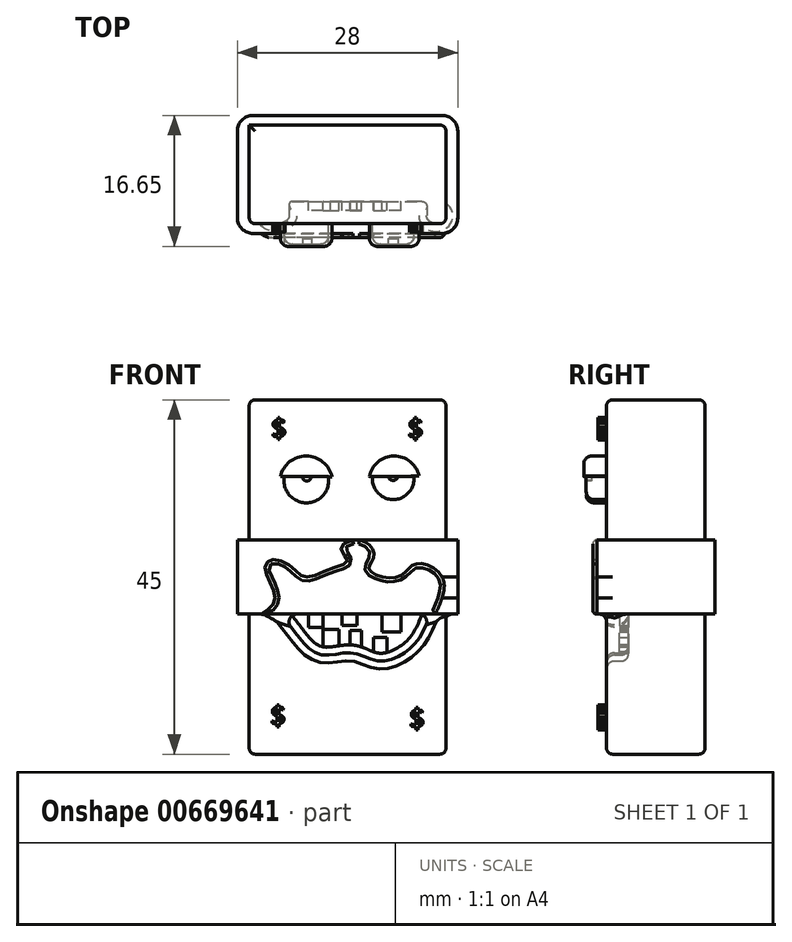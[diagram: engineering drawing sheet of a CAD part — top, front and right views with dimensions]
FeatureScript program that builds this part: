
annotation { "Feature Type Name" : "Feature", "Feature Type Description" : "" }
export const myFeature = defineFeature(function(context is Context, id is Id, definition is map)
    precondition{}
    {
        {
            var Q0;
            Q0=qCreatedBy(makeId("Front.planeOp"),FACE);
            var sketch = newSketch(context, id + "F0", { "sketchPlane" : qUnion([Q0])});
            skLineSegment(sketch, "E0.bottom", {"start": v(12.5, 22.5) * mm, "end": v(-12.5, 22.5) * mm});
            skLineSegment(sketch, "E0.top", {"start": v(12.5, -22.5) * mm, "end": v(-12.5, -22.5) * mm});
            skLineSegment(sketch, "E0.left", {"start": v(12.5, 22.5) * mm, "end": v(12.5, -22.5) * mm});
            skLineSegment(sketch, "E0.right", {"start": v(-12.5, 22.5) * mm, "end": v(-12.5, -22.5) * mm});
            skPoint(sketch, "E0.middle", {"position": v(0, 0) * mm});
            skSolve(sketch);
        }
        {
            var Q0;
            Q0=makeQuery(id+"F0.imprint","IMPRINT",FACE,{"disambiguationData":[TD([[makeQuery(id+"F0.imprint","IMPRINT",EDGE,{"derivedFrom":sQuery(id+"F0.wireOp",EDGE,"E0.bottom")}),1.0]])]});
            extrude(context, id + "F1", {"entities" : qUnion([Q0]), "endBound" : BoundingType.SYMMETRIC, "depth" : 12.5 * mm, "offsetDistance" : 25 * mm});
        }
        {
            var Q0;
            Q0=qCreatedBy(makeId("Top.planeOp"),FACE);
            var sketch = newSketch(context, id + "F2", { "sketchPlane" : qUnion([Q0])});
            skLineSegment(sketch, "E1.bottom", {"start": v(14, 7.5) * mm, "end": v(-14, 7.5) * mm});
            skLineSegment(sketch, "E1.top", {"start": v(14, -7.5) * mm, "end": v(-14, -7.5) * mm});
            skLineSegment(sketch, "E1.left", {"start": v(14, 7.5) * mm, "end": v(14, -7.5) * mm});
            skLineSegment(sketch, "E1.right", {"start": v(-14, 7.5) * mm, "end": v(-14, -7.5) * mm});
            skPoint(sketch, "E1.middle", {"position": v(0, 0) * mm});
            skSolve(sketch);
        }
        {
            var Q0;
            Q0=makeQuery(id+"F2.imprint","IMPRINT",FACE,{"disambiguationData":[TD([[makeQuery(id+"F2.imprint","IMPRINT",EDGE,{"derivedFrom":sQuery(id+"F2.wireOp",EDGE,"E1.bottom")}),1.0]])]});
            extrude(context, id + "F3", {"entities" : qUnion([Q0]), "operationType" : NewBodyOperationType.ADD, "endBound" : BoundingType.SYMMETRIC, "depth" : 9.4 * mm, "offsetDistance" : 25 * mm});
        }
        {
            var Q0;
            {var subQ0=sQuery(id+"F0.wireOp",EDGE,"E0.bottom");var subQ1=sQuery(id+"F0.wireOp",EDGE,"E0.right");var subQ2=sQuery(id+"F0.wireOp",EDGE,"E0.left");Q0=makeQuery(id+"F3.boolean.opBoolean","SPLIT",FACE,{"disambiguationData":[TD([makeQuery(id+"F1.opExtrude","SWEPT_FACE",FACE,{"disambiguationData":[OSD([subQ0])]})])],"derivedFrom":makeQuery(id+"F1.opExtrude","CAP_FACE",FACE,{"disambiguationData":[OSD([subQ0,sQuery(id+"F0.wireOp",EDGE,"E0.top"),subQ2,subQ1])],"isStart":false})});}
            var sketch = newSketch(context, id + "F4", { "sketchPlane" : qUnion([Q0])});
            skLineSegment(sketch, "E2", {"start": v(-8.04, 12.75) * mm, "end": v(-2.44, 12.75) * mm});
            skArc(sketch, "E3", {"start": v(-8.04, 12.75) * mm, "mid": v(-5.24, 9.43) * mm, "end": v(-2.44, 12.75) * mm});
            skLineSegment(sketch, "E4", {"start": v(3.15, 12.75) * mm, "end": v(8.44, 12.75) * mm});
            skArc(sketch, "E5", {"start": v(3.15, 12.75) * mm, "mid": v(5.8, 9.84) * mm, "end": v(8.44, 12.75) * mm});
            skSolve(sketch);
        }
        {
            var Q0;
            Q0=makeQuery(id+"F4.imprint","IMPRINT",FACE,{"disambiguationData":[TD([[makeQuery(id+"F4.imprint","IMPRINT",EDGE,{"derivedFrom":sQuery(id+"F4.wireOp",EDGE,"E2")}),-1.0]])]});
            var Q1;
            Q1=makeQuery(id+"F4.imprint","IMPRINT",FACE,{"disambiguationData":[TD([[makeQuery(id+"F4.imprint","IMPRINT",EDGE,{"derivedFrom":sQuery(id+"F4.wireOp",EDGE,"E4")}),-1.0]])]});
            extrude(context, id + "F5", {"entities" : qUnion([Q0, Q1]), "operationType" : NewBodyOperationType.ADD, "depth" : 2.6 * mm, "offsetDistance" : 25 * mm});
        }
        {
            var Q0;
            Q0=makeQuery(id+"F5.opExtrude","CAP_EDGE",EDGE,{"disambiguationData":[OSD([sQuery(id+"F4.wireOp",EDGE,"E3")])],"isStart":false});
            var Q1;
            Q1=makeQuery(id+"F5.opExtrude","CAP_EDGE",EDGE,{"disambiguationData":[OSD([sQuery(id+"F4.wireOp",EDGE,"E5")])],"isStart":false});
            fillet(context, id + "F6", {"entities" : qUnion([Q0, Q1]), "radius" : 1 * mm, "tangentPropagation" : true, "allowEdgeOverflow" : false});
        }
        {
            var Q0;
            {var subQ0=sQuery(id+"F0.wireOp",EDGE,"E0.bottom");var subQ1=sQuery(id+"F0.wireOp",EDGE,"E0.right");var subQ2=sQuery(id+"F0.wireOp",EDGE,"E0.left");Q0=makeQuery(id+"F3.boolean.opBoolean","SPLIT",FACE,{"disambiguationData":[TD([makeQuery(id+"F1.opExtrude","SWEPT_FACE",FACE,{"disambiguationData":[OSD([subQ0])]})])],"derivedFrom":makeQuery(id+"F1.opExtrude","CAP_FACE",FACE,{"disambiguationData":[OSD([subQ0,sQuery(id+"F0.wireOp",EDGE,"E0.top"),subQ2,subQ1])],"isStart":false})});}
            var sketch = newSketch(context, id + "F7", { "sketchPlane" : qUnion([Q0])});
            skArc(sketch, "E6", {"start": v(-2, 12.72) * mm, "mid": v(-5.25, 15.38) * mm, "end": v(-8.54, 12.75) * mm});
            skArc(sketch, "E7", {"start": v(9.08, 12.85) * mm, "mid": v(5.89, 15.37) * mm, "end": v(2.77, 12.76) * mm});
            skLineSegment(sketch, "E8", {"start": v(-8.54, 12.75) * mm, "end": v(-2, 12.72) * mm});
            skLineSegment(sketch, "E9", {"start": v(2.77, 12.76) * mm, "end": v(9.08, 12.85) * mm});
            skSolve(sketch);
        }
        {
            var Q0;
            Q0=makeQuery(id+"F7.imprint","IMPRINT",FACE,{"disambiguationData":[TD([[makeQuery(id+"F7.imprint","IMPRINT",EDGE,{"derivedFrom":sQuery(id+"F7.wireOp",EDGE,"E6")}),1.0]])]});
            var Q1;
            Q1=makeQuery(id+"F7.imprint","IMPRINT",FACE,{"disambiguationData":[TD([[makeQuery(id+"F7.imprint","IMPRINT",EDGE,{"derivedFrom":sQuery(id+"F7.wireOp",EDGE,"E7")}),1.0]])]});
            extrude(context, id + "F8", {"entities" : qUnion([Q0, Q1]), "operationType" : NewBodyOperationType.ADD, "depth" : 2.9 * mm, "offsetDistance" : 25 * mm});
        }
        {
            var Q0;
            Q0=makeQuery(id+"F8.opExtrude","CAP_EDGE",EDGE,{"disambiguationData":[OSD([sQuery(id+"F7.wireOp",EDGE,"E6")])],"isStart":false});
            var Q1;
            Q1=makeQuery(id+"F8.opExtrude","CAP_EDGE",EDGE,{"disambiguationData":[OSD([sQuery(id+"F7.wireOp",EDGE,"E7")])],"isStart":false});
            fillet(context, id + "F9", {"entities" : qUnion([Q0, Q1]), "radius" : 1 * mm, "tangentPropagation" : true, "allowEdgeOverflow" : false});
        }
        {
            var Q0;
            Q0=makeQuery(id+"F3.opExtrude","SWEPT_FACE",FACE,{"disambiguationData":[OSD([sQuery(id+"F2.wireOp",EDGE,"E1.top")])]});
            var sketch = newSketch(context, id + "F10", { "sketchPlane" : qUnion([Q0])});
            skFitSpline(sketch, "E10", {"points": [v(-10.94, -4.7) * mm, v(-9.33, -3.23) * mm, v(-9.64, -1.12) * mm, v(-10.5, 1.3) * mm, v(-9.52, 2.22) * mm, v(-7.04, 1.23) * mm, v(-5.37, 0) * mm, v(-2.34, 0.98) * mm, v(0, 2.1) * mm, v(-0.85, 3.64) * mm, v(1.5, 4.7) * mm, v(3.35, 2.78) * mm, v(2.74, 0.98) * mm, v(6.33, 0) * mm, v(8.61, 1.66) * mm, v(12.02, 0) * mm, v(11.15, -4.7) * mm], "startDerivative": vector(35.96, 23.06) * mm, "endDerivative": vector(-27.48, -60.57) * mm});
            skLineSegment(sketch, "E11", {"start": v(-10.94, -4.7) * mm, "end": v(11.15, -4.7) * mm});
            skSolve(sketch);
        }
        {
            var Q0;
            {var subQ0=sQuery(id+"F10.wireOp",EDGE,"E11");Q0=makeQuery(id+"F10.imprint","IMPRINT",FACE,{"disambiguationData":[TD([[makeQuery(id+"F10.imprint","IMPRINT",EDGE,{"derivedFrom":subQ0}),-1.0]])]});}
            extrude(context, id + "F11", {"entities" : qUnion([Q0]), "operationType" : NewBodyOperationType.ADD, "depth" : 0.5 * mm, "offsetDistance" : 25 * mm});
        }
        {
            var Q0;
            Q0=makeQuery(id+"F11.opExtrude","CAP_FACE",FACE,{"disambiguationData":[OSD([sQuery(id+"F2.wireOp",EDGE,"E1.top"),sQuery(id+"F10.wireOp",EDGE,"E10"),sQuery(id+"F10.wireOp",EDGE,"E11")])],"isStart":false});
            fillet(context, id + "F12", {"entities" : qUnion([Q0]), "radius" : .5 * mm, "tangentPropagation" : true, "allowEdgeOverflow" : false});
        }
        {
            var Q0;
            {var subQ0=sQuery(id+"F0.wireOp",EDGE,"E0.top");var subQ1=sQuery(id+"F0.wireOp",EDGE,"E0.left");var subQ2=sQuery(id+"F0.wireOp",EDGE,"E0.right");Q0=makeQuery(id+"F3.boolean.opBoolean","SPLIT",FACE,{"disambiguationData":[TD([makeQuery(id+"F1.opExtrude","SWEPT_FACE",FACE,{"disambiguationData":[OSD([subQ0])]})])],"derivedFrom":makeQuery(id+"F1.opExtrude","CAP_FACE",FACE,{"disambiguationData":[OSD([sQuery(id+"F0.wireOp",EDGE,"E0.bottom"),subQ0,subQ1,subQ2])],"isStart":false})});}
            var sketch = newSketch(context, id + "F13", { "sketchPlane" : qUnion([Q0])});
            skFitSpline(sketch, "E12", {"points": [v(-8.5, -4.7) * mm, v(-6.6, -7.12) * mm, v(-3.55, -9.81) * mm, v(0.62, -9.64) * mm, v(4, -10.68) * mm, v(8.35, -8.68) * mm, v(10.52, -4.7) * mm], "startDerivative": vector(12.32, -15.33) * mm, "endDerivative": vector(8.9, 23.95) * mm});
            skLineSegment(sketch, "E13", {"start": v(-8.5, -4.7) * mm, "end": v(10.52, -4.7) * mm});
            skSolve(sketch);
        }
        {
            var Q0;
            Q0=makeQuery(id+"F13.imprint","IMPRINT",FACE,{"disambiguationData":[TD([[makeQuery(id+"F13.imprint","IMPRINT",EDGE,{"derivedFrom":sQuery(id+"F13.wireOp",EDGE,"E12")}),1.0]])]});
            extrude(context, id + "F14", {"entities" : qUnion([Q0]), "operationType" : NewBodyOperationType.REMOVE, "oppositeDirection" : true, "depth" : 2.8 * mm, "offsetDistance" : 25 * mm});
        }
        {
            var Q0;
            Q0=makeQuery(id+"F14.boolean.opBoolean","COPY",FACE,{"derivedFrom":makeQuery(id+"F14.opExtrude","SWEPT_FACE",FACE,{"disambiguationData":[OSD([sQuery(id+"F13.wireOp",EDGE,"E12")])]})});
            fillet(context, id + "F15", {"entities" : qUnion([Q0]), "radius" : 1 * mm, "tangentPropagation" : true, "allowEdgeOverflow" : false});
        }
        {
            var Q0;
            Q0=makeQuery(id+"F14.boolean.opBoolean","COPY",FACE,{"derivedFrom":makeQuery(id+"F14.opExtrude","CAP_FACE",FACE,{"disambiguationData":[OSD([sQuery(id+"F13.wireOp",EDGE,"E12"),sQuery(id+"F13.wireOp",EDGE,"E13")])],"isStart":false})});
            var sketch = newSketch(context, id + "F16", { "sketchPlane" : qUnion([Q0])});
            skLineSegment(sketch, "E14", {"start": v(-4.96, -4.7) * mm, "end": v(-4.96, -6.43) * mm});
            skLineSegment(sketch, "E15", {"start": v(-4.96, -6.43) * mm, "end": v(-3.1, -6.43) * mm});
            skLineSegment(sketch, "E16", {"start": v(-3.1, -6.43) * mm, "end": v(-3.1, -4.7) * mm});
            skLineSegment(sketch, "E17", {"start": v(-3.1, -4.7) * mm, "end": v(-4.96, -4.7) * mm});
            skLineSegment(sketch, "E18.bottom", {"start": v(-0.73, -4.7) * mm, "end": v(1.22, -4.7) * mm});
            skLineSegment(sketch, "E18.top", {"start": v(-0.73, -6.16) * mm, "end": v(1.22, -6.16) * mm});
            skLineSegment(sketch, "E18.left", {"start": v(-0.73, -4.7) * mm, "end": v(-0.73, -6.16) * mm});
            skLineSegment(sketch, "E18.right", {"start": v(1.22, -4.7) * mm, "end": v(1.22, -6.16) * mm});
            skLineSegment(sketch, "E19.bottom", {"start": v(4.38, -4.7) * mm, "end": v(6.78, -4.7) * mm});
            skLineSegment(sketch, "E19.top", {"start": v(4.38, -6.98) * mm, "end": v(6.78, -6.98) * mm});
            skLineSegment(sketch, "E19.left", {"start": v(4.38, -4.7) * mm, "end": v(4.38, -6.98) * mm});
            skLineSegment(sketch, "E19.right", {"start": v(6.78, -4.7) * mm, "end": v(6.78, -6.98) * mm});
            skLineSegment(sketch, "E20.bottom", {"start": v(-3.1, -8.89) * mm, "end": v(-1.11, -8.89) * mm});
            skLineSegment(sketch, "E20.top", {"start": v(-3.1, -6.68) * mm, "end": v(-1.11, -6.68) * mm});
            skLineSegment(sketch, "E20.left", {"start": v(-3.1, -8.89) * mm, "end": v(-3.1, -6.68) * mm});
            skLineSegment(sketch, "E20.right", {"start": v(-1.11, -8.89) * mm, "end": v(-1.11, -6.68) * mm});
            skLineSegment(sketch, "E21.bottom", {"start": v(1.78, -9.07) * mm, "end": v(0.28, -9.07) * mm});
            skLineSegment(sketch, "E21.top", {"start": v(1.78, -6.79) * mm, "end": v(0.28, -6.79) * mm});
            skLineSegment(sketch, "E21.left", {"start": v(1.78, -9.07) * mm, "end": v(1.78, -6.79) * mm});
            skLineSegment(sketch, "E21.right", {"start": v(0.28, -9.07) * mm, "end": v(0.28, -6.79) * mm});
            skLineSegment(sketch, "E22.bottom", {"start": v(3.3, -9.76) * mm, "end": v(4.99, -9.76) * mm});
            skLineSegment(sketch, "E22.top", {"start": v(3.3, -7.65) * mm, "end": v(4.99, -7.65) * mm});
            skLineSegment(sketch, "E22.left", {"start": v(3.3, -9.76) * mm, "end": v(3.3, -7.65) * mm});
            skLineSegment(sketch, "E22.right", {"start": v(4.99, -9.76) * mm, "end": v(4.99, -7.65) * mm});
            skSolve(sketch);
        }
        {
            var Q0;
            Q0=makeQuery(id+"F16.imprint","IMPRINT",FACE,{"disambiguationData":[TD([[makeQuery(id+"F16.imprint","IMPRINT",EDGE,{"derivedFrom":sQuery(id+"F16.wireOp",EDGE,"E14")}),1.0]])]});
            var Q1;
            {var subQ1=sQuery(id+"F16.wireOp",EDGE,"E20.top");Q1=makeQuery(id+"F16.imprint","IMPRINT",FACE,{"disambiguationData":[TD([[makeQuery(id+"F16.imprint","IMPRINT",EDGE,{"derivedFrom":subQ1}),-1.0]])]});}
            var Q2;
            Q2=makeQuery(id+"F16.imprint","IMPRINT",FACE,{"disambiguationData":[TD([[makeQuery(id+"F16.imprint","IMPRINT",EDGE,{"derivedFrom":sQuery(id+"F16.wireOp",EDGE,"E18.bottom")}),1.0]])]});
            var Q3;
            {var subQ0=sQuery(id+"F16.wireOp",EDGE,"E21.top");Q3=makeQuery(id+"F16.imprint","IMPRINT",FACE,{"disambiguationData":[TD([[makeQuery(id+"F16.imprint","IMPRINT",EDGE,{"derivedFrom":subQ0}),1.0]])]});}
            var Q4;
            {var subQ0=sQuery(id+"F16.wireOp",EDGE,"E22.top");Q4=makeQuery(id+"F16.imprint","IMPRINT",FACE,{"disambiguationData":[TD([[makeQuery(id+"F16.imprint","IMPRINT",EDGE,{"derivedFrom":subQ0}),-1.0]])]});}
            var Q5;
            Q5=makeQuery(id+"F16.imprint","IMPRINT",FACE,{"disambiguationData":[TD([[makeQuery(id+"F16.imprint","IMPRINT",EDGE,{"derivedFrom":sQuery(id+"F16.wireOp",EDGE,"E19.bottom")}),1.0]])]});
            extrude(context, id + "F17", {"entities" : qUnion([Q0, Q1, Q2, Q3, Q4, Q5]), "operationType" : NewBodyOperationType.ADD, "depth" : 1.14 * mm, "offsetDistance" : 25 * mm});
        }
        {
            var Q0;
            Q0=makeQuery(id+"F5.opExtrude","CAP_FACE",FACE,{"disambiguationData":[OSD([sQuery(id+"F4.wireOp",EDGE,"E2"),sQuery(id+"F4.wireOp",EDGE,"E3")])],"isStart":false});
            var sketch = newSketch(context, id + "F18", { "sketchPlane" : qUnion([Q0])});
            skArc(sketch, "E23", {"start": v(-5.74, 12.75) * mm, "mid": v(-5.18, 12.2) * mm, "end": v(-4.61, 12.75) * mm});
            skArc(sketch, "E24", {"start": v(5.15, 12.75) * mm, "mid": v(5.78, 12.27) * mm, "end": v(6.4, 12.75) * mm});
            skLineSegment(sketch, "E25", {"start": v(-5.74, 12.75) * mm, "end": v(-4.61, 12.75) * mm});
            skLineSegment(sketch, "E26", {"start": v(5.15, 12.75) * mm, "end": v(6.4, 12.75) * mm});
            skSolve(sketch);
        }
        {
            var Q0;
            Q0=makeQuery(id+"F18.imprint","IMPRINT",FACE,{"disambiguationData":[TD([[makeQuery(id+"F18.imprint","IMPRINT",EDGE,{"derivedFrom":sQuery(id+"F18.wireOp",EDGE,"E23")}),1.0]])]});
            var Q1;
            Q1=makeQuery(id+"F18.imprint","IMPRINT",FACE,{"disambiguationData":[TD([[makeQuery(id+"F18.imprint","IMPRINT",EDGE,{"derivedFrom":sQuery(id+"F18.wireOp",EDGE,"E24")}),1.0]])]});
            extrude(context, id + "F19", {"entities" : qUnion([Q0, Q1]), "operationType" : NewBodyOperationType.REMOVE, "oppositeDirection" : true, "depth" : 0.69 * mm, "offsetDistance" : 25 * mm});
        }
        {
            var Q0;
            {var subQ0=sQuery(id+"F0.wireOp",EDGE,"E0.bottom");var subQ1=sQuery(id+"F0.wireOp",EDGE,"E0.right");Q0=makeQuery(id+"F3.boolean.opBoolean","SPLIT",EDGE,{"disambiguationData":[TD([makeQuery(id+"F1.opExtrude","SWEPT_FACE",FACE,{"disambiguationData":[OSD([subQ0])]})])],"derivedFrom":makeQuery(id+"F1.opExtrude","CAP_EDGE",EDGE,{"disambiguationData":[OSD([subQ1])],"isStart":false})});}
            var Q1;
            Q1=makeQuery(id+"F1.opExtrude","CAP_EDGE",EDGE,{"disambiguationData":[OSD([sQuery(id+"F0.wireOp",EDGE,"E0.bottom")])],"isStart":false});
            var Q2;
            Q2=makeQuery(id+"F1.opExtrude","SWEPT_EDGE",EDGE,{"disambiguationData":[OSD([sQuery(id+"F0.wireOp",EDGE,"E0.bottom"),sQuery(id+"F0.wireOp",EDGE,"E0.right")])]});
            var Q3;
            {var subQ0=sQuery(id+"F0.wireOp",EDGE,"E0.bottom");var subQ1=sQuery(id+"F0.wireOp",EDGE,"E0.left");Q3=makeQuery(id+"F3.boolean.opBoolean","SPLIT",EDGE,{"disambiguationData":[TD([makeQuery(id+"F1.opExtrude","SWEPT_FACE",FACE,{"disambiguationData":[OSD([subQ0])]})])],"derivedFrom":makeQuery(id+"F1.opExtrude","CAP_EDGE",EDGE,{"disambiguationData":[OSD([subQ1])],"isStart":false})});}
            var Q4;
            Q4=makeQuery(id+"F1.opExtrude","SWEPT_EDGE",EDGE,{"disambiguationData":[OSD([sQuery(id+"F0.wireOp",EDGE,"E0.bottom"),sQuery(id+"F0.wireOp",EDGE,"E0.left")])]});
            var Q5;
            {var subQ0=sQuery(id+"F0.wireOp",EDGE,"E0.bottom");var subQ1=sQuery(id+"F0.wireOp",EDGE,"E0.left");Q5=makeQuery(id+"F3.boolean.opBoolean","SPLIT",EDGE,{"disambiguationData":[TD([makeQuery(id+"F1.opExtrude","SWEPT_FACE",FACE,{"disambiguationData":[OSD([subQ0])]})])],"derivedFrom":makeQuery(id+"F1.opExtrude","CAP_EDGE",EDGE,{"disambiguationData":[OSD([subQ1])],"isStart":true})});}
            var Q6;
            Q6=makeQuery(id+"F1.opExtrude","CAP_EDGE",EDGE,{"disambiguationData":[OSD([sQuery(id+"F0.wireOp",EDGE,"E0.bottom")])],"isStart":true});
            var Q7;
            {var subQ0=sQuery(id+"F0.wireOp",EDGE,"E0.left");var subQ1=sQuery(id+"F0.wireOp",EDGE,"E0.top");Q7=makeQuery(id+"F3.boolean.opBoolean","SPLIT",EDGE,{"disambiguationData":[TD([makeQuery(id+"F1.opExtrude","SWEPT_FACE",FACE,{"disambiguationData":[OSD([subQ1])]})])],"derivedFrom":makeQuery(id+"F1.opExtrude","CAP_EDGE",EDGE,{"disambiguationData":[OSD([subQ0])],"isStart":false})});}
            var Q8;
            Q8=makeQuery(id+"F1.opExtrude","SWEPT_EDGE",EDGE,{"disambiguationData":[OSD([sQuery(id+"F0.wireOp",EDGE,"E0.top"),sQuery(id+"F0.wireOp",EDGE,"E0.left")])]});
            var Q9;
            {var subQ0=sQuery(id+"F0.wireOp",EDGE,"E0.left");var subQ1=sQuery(id+"F0.wireOp",EDGE,"E0.top");Q9=makeQuery(id+"F3.boolean.opBoolean","SPLIT",EDGE,{"disambiguationData":[TD([makeQuery(id+"F1.opExtrude","SWEPT_FACE",FACE,{"disambiguationData":[OSD([subQ1])]})])],"derivedFrom":makeQuery(id+"F1.opExtrude","CAP_EDGE",EDGE,{"disambiguationData":[OSD([subQ0])],"isStart":true})});}
            var Q10;
            Q10=makeQuery(id+"F1.opExtrude","CAP_EDGE",EDGE,{"disambiguationData":[OSD([sQuery(id+"F0.wireOp",EDGE,"E0.top")])],"isStart":true});
            var Q11;
            Q11=makeQuery(id+"F1.opExtrude","CAP_EDGE",EDGE,{"disambiguationData":[OSD([sQuery(id+"F0.wireOp",EDGE,"E0.top")])],"isStart":false});
            var Q12;
            Q12=makeQuery(id+"F1.opExtrude","SWEPT_EDGE",EDGE,{"disambiguationData":[OSD([sQuery(id+"F0.wireOp",EDGE,"E0.top"),sQuery(id+"F0.wireOp",EDGE,"E0.right")])]});
            var Q13;
            {var subQ0=sQuery(id+"F0.wireOp",EDGE,"E0.right");var subQ1=sQuery(id+"F0.wireOp",EDGE,"E0.top");Q13=makeQuery(id+"F3.boolean.opBoolean","SPLIT",EDGE,{"disambiguationData":[TD([makeQuery(id+"F1.opExtrude","SWEPT_FACE",FACE,{"disambiguationData":[OSD([subQ1])]})])],"derivedFrom":makeQuery(id+"F1.opExtrude","CAP_EDGE",EDGE,{"disambiguationData":[OSD([subQ0])],"isStart":true})});}
            var Q14;
            {var subQ0=sQuery(id+"F0.wireOp",EDGE,"E0.right");var subQ1=sQuery(id+"F0.wireOp",EDGE,"E0.top");Q14=makeQuery(id+"F3.boolean.opBoolean","SPLIT",EDGE,{"disambiguationData":[TD([makeQuery(id+"F1.opExtrude","SWEPT_FACE",FACE,{"disambiguationData":[OSD([subQ1])]})])],"derivedFrom":makeQuery(id+"F1.opExtrude","CAP_EDGE",EDGE,{"disambiguationData":[OSD([subQ0])],"isStart":false})});}
            var Q15;
            {var subQ0=sQuery(id+"F0.wireOp",EDGE,"E0.right");var subQ1=sQuery(id+"F0.wireOp",EDGE,"E0.left");var subQ2=sQuery(id+"F0.wireOp",EDGE,"E0.top");var subQ3=sQuery(id+"F0.wireOp",EDGE,"E0.bottom");var subQ4=makeQuery(id+"F1.opExtrude","CAP_FACE",FACE,{"disambiguationData":[OSD([subQ3,subQ2,subQ1,subQ0])],"isStart":false});var subQ5=makeQuery(id+"F3.opExtrude","CAP_FACE",FACE,{"disambiguationData":[OSD([sQuery(id+"F2.wireOp",EDGE,"E1.bottom"),sQuery(id+"F2.wireOp",EDGE,"E1.top"),sQuery(id+"F2.wireOp",EDGE,"E1.left"),sQuery(id+"F2.wireOp",EDGE,"E1.right")])],"isStart":true});var subQ6=makeQuery(id+"F1.opExtrude","SWEPT_FACE",FACE,{"disambiguationData":[OSD([subQ0])]});Q15=makeQuery(id+"F15.opFillet","BLEND_EDGE",EDGE,{"blendedFrom":[makeQuery(id+"F14.boolean.opBoolean","SPLIT",EDGE,{"disambiguationData":[TD([subQ6])],"derivedFrom":makeQuery(id+"F3.boolean.opBoolean","INTERSECT",EDGE,{"derivedFrom":[subQ4,subQ5]})}),makeQuery(id+"F3.boolean.opBoolean","SPLIT",FACE,{"disambiguationData":[TD([makeQuery(id+"F1.opExtrude","SWEPT_FACE",FACE,{"disambiguationData":[OSD([subQ2])]})])],"derivedFrom":subQ6})],"blendedInto":[makeQuery(id+"F3.boolean.opBoolean","SPLIT",FACE,{"disambiguationData":[TD([makeQuery(id+"F1.opExtrude","SWEPT_FACE",FACE,{"disambiguationData":[OSD([subQ2])]})])],"derivedFrom":subQ6})]});}
            fillet(context, id + "F20", {"entities" : qUnion([Q0, Q1, Q2, Q3, Q4, Q5, Q6, Q7, Q8, Q9, Q10, Q11, Q12, Q13, Q14, Q15]), "radius" : .75 * mm, "tangentPropagation" : true, "allowEdgeOverflow" : false});
        }
        {
            var Q0;
            Q0=makeQuery(id+"F3.opExtrude","SWEPT_EDGE",EDGE,{"disambiguationData":[OSD([sQuery(id+"F2.wireOp",EDGE,"E1.top"),sQuery(id+"F2.wireOp",EDGE,"E1.right")])]});
            var Q1;
            Q1=makeQuery(id+"F3.opExtrude","SWEPT_EDGE",EDGE,{"disambiguationData":[OSD([sQuery(id+"F2.wireOp",EDGE,"E1.bottom"),sQuery(id+"F2.wireOp",EDGE,"E1.right")])]});
            var Q2;
            Q2=makeQuery(id+"F3.opExtrude","SWEPT_EDGE",EDGE,{"disambiguationData":[OSD([sQuery(id+"F2.wireOp",EDGE,"E1.bottom"),sQuery(id+"F2.wireOp",EDGE,"E1.left")])]});
            var Q3;
            Q3=makeQuery(id+"F3.opExtrude","SWEPT_EDGE",EDGE,{"disambiguationData":[OSD([sQuery(id+"F2.wireOp",EDGE,"E1.top"),sQuery(id+"F2.wireOp",EDGE,"E1.left")])]});
            fillet(context, id + "F21", {"entities" : qUnion([Q0, Q1, Q2, Q3]), "radius" : 2 * mm, "tangentPropagation" : true, "allowEdgeOverflow" : false});
        }
        {
            var Q0;
            {var subQ0=sQuery(id+"F0.wireOp",EDGE,"E0.bottom");var subQ1=sQuery(id+"F0.wireOp",EDGE,"E0.right");var subQ2=sQuery(id+"F0.wireOp",EDGE,"E0.left");Q0=makeQuery(id+"F3.boolean.opBoolean","SPLIT",FACE,{"disambiguationData":[TD([makeQuery(id+"F1.opExtrude","SWEPT_FACE",FACE,{"disambiguationData":[OSD([subQ0])]})])],"derivedFrom":makeQuery(id+"F1.opExtrude","CAP_FACE",FACE,{"disambiguationData":[OSD([subQ0,sQuery(id+"F0.wireOp",EDGE,"E0.top"),subQ2,subQ1])],"isStart":false})});}
            var sketch = newSketch(context, id + "F22", { "sketchPlane" : qUnion([Q0])});
            skText(sketch, "E27", { "text": "$", "fontName": "OpenSans-Regular.ttf"});
            skText(sketch, "E28", { "text": "$", "fontName": "OpenSans-Regular.ttf"});
            skText(sketch, "E29", { "text": "$", "fontName": "OpenSans-Regular.ttf"});
            skText(sketch, "E30", { "text": "$", "fontName": "OpenSans-Regular.ttf"});
            const initialGuessF22  = {"E27": [-0.00971, 0.01765, 1, 0, 0.00248], "E28": [0.00765, 0.01763, 1, 0, 0.00248], "E29": [-0.00982, -0.01883, 1, 0, 0.00248], "E30": [0.00784, -0.0192, 1, 0, 0.00248]};
            skSetInitialGuess(sketch, initialGuessF22);
            skSolve(sketch);
        }
        {
            var Q0;
            Q0 = qSketchRegion(id + "F22", true);
            extrude(context, id + "F23", {"entities" : qUnion([Q0]), "operationType" : NewBodyOperationType.ADD, "depth" : 1.1 * mm, "offsetDistance" : 25 * mm});
        }
    });
